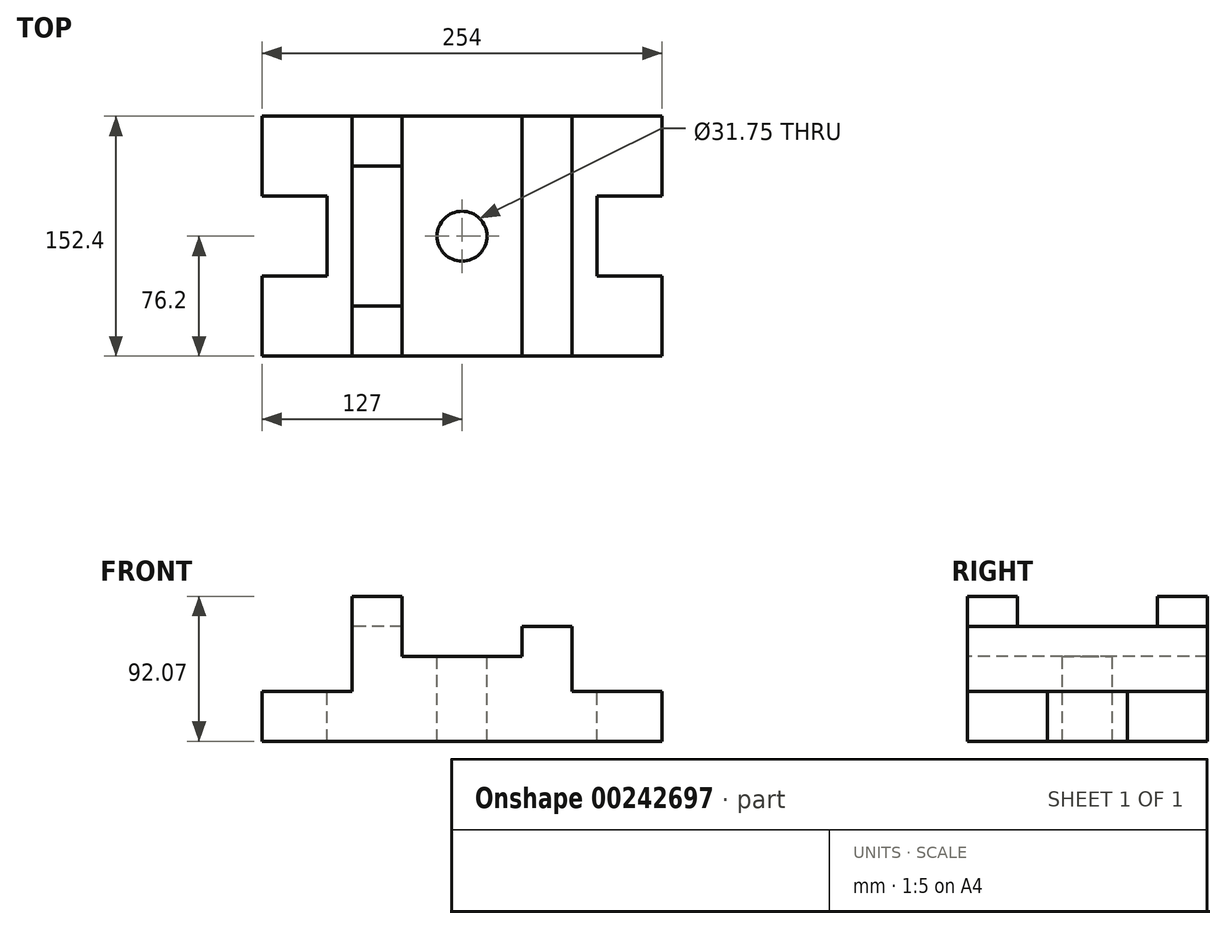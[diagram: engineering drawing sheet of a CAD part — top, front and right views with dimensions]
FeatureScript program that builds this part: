
annotation { "Feature Type Name" : "Feature", "Feature Type Description" : "" }
export const myFeature = defineFeature(function(context is Context, id is Id, definition is map)
    precondition{}
    {
        {
            var Q0;
            Q0=qCreatedBy(makeId("Top.planeOp"),FACE);
            var sketch = newSketch(context, id + "F0", { "sketchPlane" : qUnion([Q0])});
            skLineSegment(sketch, "E0.bottom", {"start": v(127, 76.2) * mm, "end": v(-127, 76.2) * mm});
            skLineSegment(sketch, "E0.top", {"start": v(127, -76.2) * mm, "end": v(-127, -76.2) * mm});
            skLineSegment(sketch, "E0.left", {"start": v(127, 76.2) * mm, "end": v(127, -76.2) * mm});
            skLineSegment(sketch, "E0.right", {"start": v(-127, 76.2) * mm, "end": v(-127, -76.2) * mm});
            skPoint(sketch, "E0.middle", {"position": v(0, 0) * mm});
            skLineSegment(sketch, "E1.bottom", {"start": v(127, 0) * mm, "end": v(85.72, 0) * mm});
            skLineSegment(sketch, "E1.top", {"start": v(127, 25.4) * mm, "end": v(85.72, 25.4) * mm});
            skLineSegment(sketch, "E1.left", {"start": v(127, 0) * mm, "end": v(127, 25.4) * mm});
            skLineSegment(sketch, "E1.right", {"start": v(85.72, 0) * mm, "end": v(85.72, 25.4) * mm});
            skPoint(sketch, "E2.oppositeSnap0", {"position": v(85.72, 12.7) * mm});
            skLineSegment(sketch, "E2.top", {"start": v(127, -25.4) * mm, "end": v(85.72, -25.4) * mm});
            skLineSegment(sketch, "E2.left", {"start": v(127, 0) * mm, "end": v(127, -25.4) * mm});
            skLineSegment(sketch, "E2.right", {"start": v(85.72, 0) * mm, "end": v(85.72, -25.4) * mm});
            skLineSegment(sketch, "E3", {"start": v(0, 76.2) * mm, "end": v(0, -76.2) * mm, "construction": true});
            skLineSegment(sketch, "E4", {"start": v(127, 76.2) * mm, "end": v(69.85, 76.2) * mm, "construction": true});
            skLineSegment(sketch, "E5.bottom", {"start": v(69.85, 76.2) * mm, "end": v(38.1, 76.2) * mm});
            skLineSegment(sketch, "E5.top", {"start": v(69.85, -76.2) * mm, "end": v(38.1, -76.2) * mm});
            skLineSegment(sketch, "E5.left", {"start": v(69.85, 76.2) * mm, "end": v(69.85, -76.2) * mm});
            skLineSegment(sketch, "E5.right", {"start": v(38.1, 76.2) * mm, "end": v(38.1, -76.2) * mm});
            skLineSegment(sketch, "E6", {"start": v(38.1, 76.2) * mm, "end": v(38.1, 44.45) * mm});
            skLineSegment(sketch, "E7", {"start": v(38.1, 44.45) * mm, "end": v(69.85, 44.45) * mm});
            skLineSegment(sketch, "E8", {"start": v(38.1, -76.2) * mm, "end": v(38.1, -44.45) * mm});
            skLineSegment(sketch, "E9", {"start": v(38.1, -44.45) * mm, "end": v(69.85, -44.45) * mm});
            skLineSegment(sketch, "E10.MirrorCS", {"start": v(-38.1, 76.2) * mm, "end": v(-38.1, 44.45) * mm});
            skLineSegment(sketch, "E11.MirrorCS", {"start": v(-38.1, 44.45) * mm, "end": v(-69.85, 44.45) * mm});
            skLineSegment(sketch, "E12.MirrorCS", {"start": v(-69.85, 76.2) * mm, "end": v(-69.85, -76.2) * mm});
            skLineSegment(sketch, "E13.MirrorCS", {"start": v(-38.1, 76.2) * mm, "end": v(-38.1, -76.2) * mm});
            skLineSegment(sketch, "E14.MirrorCS", {"start": v(-38.1, -44.45) * mm, "end": v(-69.85, -44.45) * mm});
            skLineSegment(sketch, "E15.MirrorCS", {"start": v(-38.1, -76.2) * mm, "end": v(-38.1, -44.45) * mm});
            skLineSegment(sketch, "E16.MirrorCS", {"start": v(-127, 25.4) * mm, "end": v(-85.72, 25.4) * mm});
            skLineSegment(sketch, "E17.MirrorCS", {"start": v(-85.72, 0) * mm, "end": v(-85.72, 25.4) * mm});
            skLineSegment(sketch, "E18.MirrorCS", {"start": v(-85.72, 0) * mm, "end": v(-85.72, -25.4) * mm});
            skLineSegment(sketch, "E19.MirrorCS", {"start": v(-127, -25.4) * mm, "end": v(-85.72, -25.4) * mm});
            skLineSegment(sketch, "E20.MirrorCS", {"start": v(-127, 0) * mm, "end": v(-85.72, 0) * mm});
            skCircle(sketch, "E21", {"center": v(0, 0) * mm, "radius": 15.88 * mm});
            skSolve(sketch);
        }
        {
            var Q0;
            {var subQ5=sQuery(id+"F0.wireOp",EDGE,"E16.MirrorCS");Q0=makeQuery(id+"F0.imprint","IMPRINT",FACE,{"disambiguationData":[TD([[makeQuery(id+"F0.imprint","IMPRINT",EDGE,{"derivedFrom":subQ5}),1.0]])]});}
            var Q1;
            {var subQ5=sQuery(id+"F0.wireOp",EDGE,"E11.MirrorCS");Q1=makeQuery(id+"F0.imprint","IMPRINT",FACE,{"disambiguationData":[TD([[makeQuery(id+"F0.imprint","IMPRINT",EDGE,{"derivedFrom":subQ5}),-1.0]])]});}
            var Q2;
            {var subQ0=sQuery(id+"F0.wireOp",EDGE,"E11.MirrorCS");Q2=makeQuery(id+"F0.imprint","IMPRINT",FACE,{"disambiguationData":[TD([[makeQuery(id+"F0.imprint","IMPRINT",EDGE,{"derivedFrom":subQ0}),1.0]])]});}
            var Q3;
            {var subQ4=sQuery(id+"F0.wireOp",EDGE,"E14.MirrorCS");Q3=makeQuery(id+"F0.imprint","IMPRINT",FACE,{"disambiguationData":[TD([[makeQuery(id+"F0.imprint","IMPRINT",EDGE,{"derivedFrom":subQ4}),1.0]])]});}
            var Q4;
            Q4=makeQuery(id+"F0.imprint","IMPRINT",FACE,{"disambiguationData":[TD([[makeQuery(id+"F0.imprint","IMPRINT",EDGE,{"derivedFrom":sQuery(id+"F0.wireOp",EDGE,"E5.right")}),-1.0]])]});
            var Q5;
            {var subQ0=sQuery(id+"F0.wireOp",EDGE,"E5.top");Q5=makeQuery(id+"F0.imprint","IMPRINT",FACE,{"disambiguationData":[TD([[makeQuery(id+"F0.imprint","IMPRINT",EDGE,{"derivedFrom":subQ0}),-1.0]])]});}
            var Q6;
            Q6=makeQuery(id+"F0.imprint","IMPRINT",FACE,{"disambiguationData":[TD([[makeQuery(id+"F0.imprint","IMPRINT",EDGE,{"derivedFrom":sQuery(id+"F0.wireOp",EDGE,"E5.right")}),1.0]])]});
            var Q7;
            {var subQ0=sQuery(id+"F0.wireOp",EDGE,"E5.bottom");Q7=makeQuery(id+"F0.imprint","IMPRINT",FACE,{"disambiguationData":[TD([[makeQuery(id+"F0.imprint","IMPRINT",EDGE,{"derivedFrom":subQ0}),1.0]])]});}
            var Q8;
            {var subQ7=sQuery(id+"F0.wireOp",EDGE,"E1.top");Q8=makeQuery(id+"F0.imprint","IMPRINT",FACE,{"disambiguationData":[TD([[makeQuery(id+"F0.imprint","IMPRINT",EDGE,{"derivedFrom":subQ7}),-1.0]])]});}
            extrude(context, id + "F1", {"entities" : qUnion([Q0, Q1, Q2, Q3, Q4, Q5, Q6, Q7, Q8]), "oppositeDirection" : true, "depth" : 31.75 * mm});
        }
        {
            var Q0;
            {var subQ5=sQuery(id+"F0.wireOp",EDGE,"E11.MirrorCS");Q0=makeQuery(id+"F0.imprint","IMPRINT",FACE,{"disambiguationData":[TD([[makeQuery(id+"F0.imprint","IMPRINT",EDGE,{"derivedFrom":subQ5}),-1.0]])]});}
            var Q1;
            {var subQ4=sQuery(id+"F0.wireOp",EDGE,"E14.MirrorCS");Q1=makeQuery(id+"F0.imprint","IMPRINT",FACE,{"disambiguationData":[TD([[makeQuery(id+"F0.imprint","IMPRINT",EDGE,{"derivedFrom":subQ4}),1.0]])]});}
            var Q2;
            {var subQ0=sQuery(id+"F0.wireOp",EDGE,"E5.bottom");Q2=makeQuery(id+"F0.imprint","IMPRINT",FACE,{"disambiguationData":[TD([[makeQuery(id+"F0.imprint","IMPRINT",EDGE,{"derivedFrom":subQ0}),1.0]])]});}
            var Q3;
            {var subQ0=sQuery(id+"F0.wireOp",EDGE,"E5.top");Q3=makeQuery(id+"F0.imprint","IMPRINT",FACE,{"disambiguationData":[TD([[makeQuery(id+"F0.imprint","IMPRINT",EDGE,{"derivedFrom":subQ0}),-1.0]])]});}
            extrude(context, id + "F2", {"entities" : qUnion([Q0, Q1, Q2, Q3]), "operationType" : NewBodyOperationType.ADD, "depth" : 60.32 * mm});
        }
        {
            var Q0;
            {var subQ0=sQuery(id+"F0.wireOp",EDGE,"E11.MirrorCS");Q0=makeQuery(id+"F0.imprint","IMPRINT",FACE,{"disambiguationData":[TD([[makeQuery(id+"F0.imprint","IMPRINT",EDGE,{"derivedFrom":subQ0}),1.0]])]});}
            var Q1;
            Q1=makeQuery(id+"F0.imprint","IMPRINT",FACE,{"disambiguationData":[TD([[makeQuery(id+"F0.imprint","IMPRINT",EDGE,{"derivedFrom":sQuery(id+"F0.wireOp",EDGE,"E5.right")}),1.0]])]});
            extrude(context, id + "F3", {"entities" : qUnion([Q0, Q1]), "operationType" : NewBodyOperationType.ADD, "depth" : 41.27 * mm});
        }
        {
            var Q0;
            Q0=makeQuery(id+"F0.imprint","IMPRINT",FACE,{"disambiguationData":[TD([[makeQuery(id+"F0.imprint","IMPRINT",EDGE,{"derivedFrom":sQuery(id+"F0.wireOp",EDGE,"E5.right")}),-1.0]])]});
            extrude(context, id + "F4", {"entities" : qUnion([Q0]), "operationType" : NewBodyOperationType.ADD, "depth" : 22.22 * mm});
        }
    });
